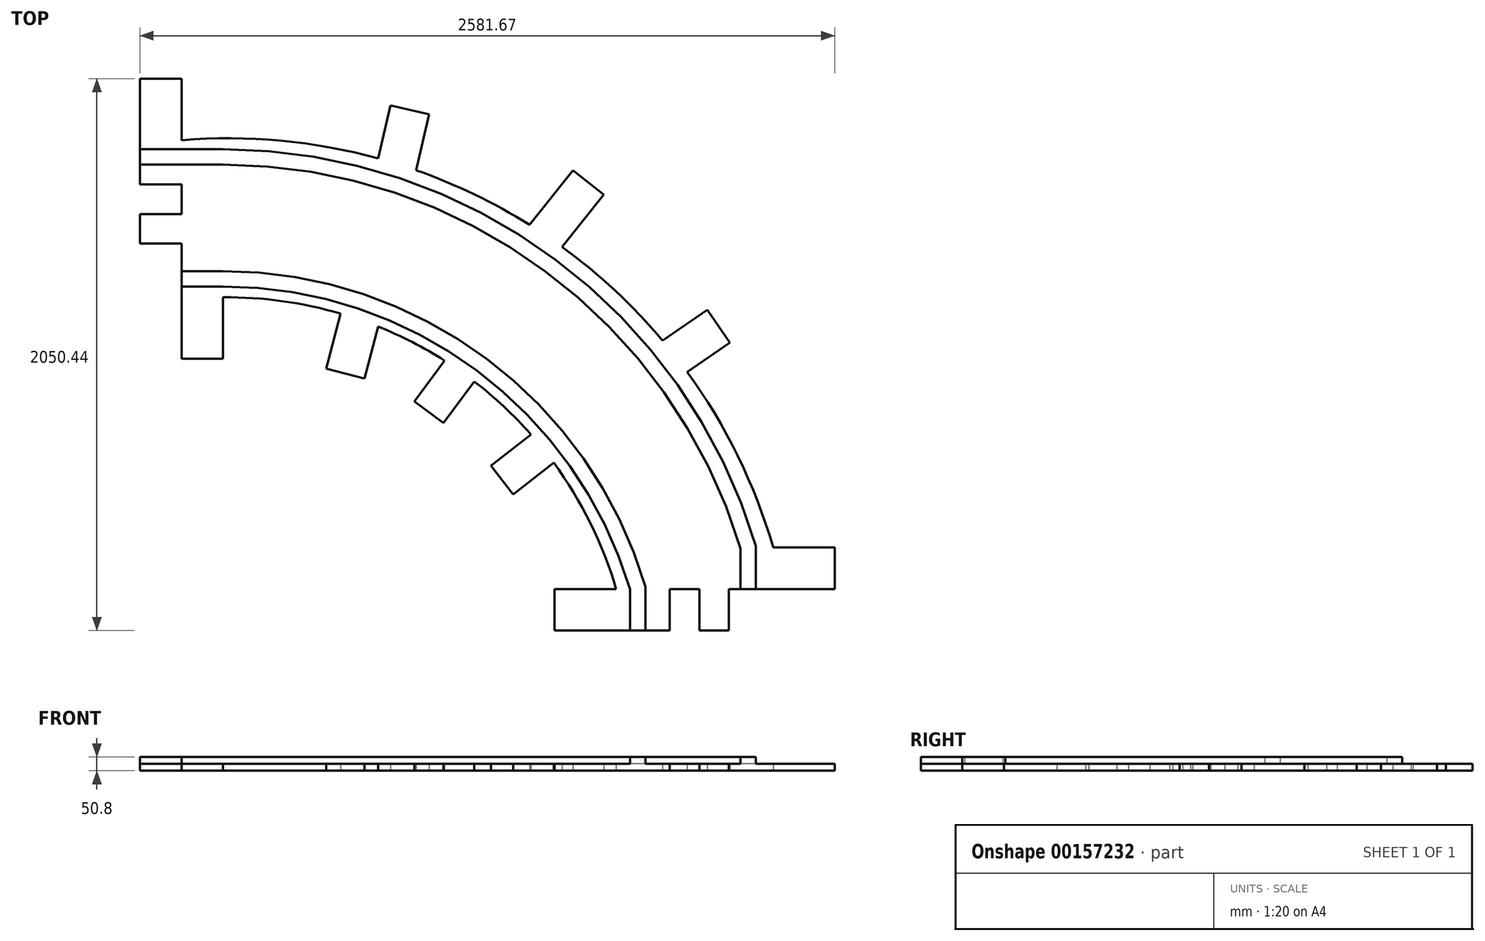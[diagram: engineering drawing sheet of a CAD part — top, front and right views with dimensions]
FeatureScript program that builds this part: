
annotation { "Feature Type Name" : "Feature", "Feature Type Description" : "" }
export const myFeature = defineFeature(function(context is Context, id is Id, definition is map)
    precondition{}
    {
        {
            var Q0;
            Q0=qCreatedBy(makeId("Top.planeOp"),FACE);
            var sketch = newSketch(context, id + "F0", { "sketchPlane" : qUnion([Q0])});
            skLineSegment(sketch, "E0", {"start": v(-123.12, 340.2) * mm, "end": v(-123.12, -52.81) * mm});
            skLineSegment(sketch, "E1", {"start": v(-123.12, -52.81) * mm, "end": v(31.19, -52.81) * mm});
            skLineSegment(sketch, "E2", {"start": v(31.19, -52.81) * mm, "end": v(31.19, -162.82) * mm});
            skLineSegment(sketch, "E3", {"start": v(31.19, -162.82) * mm, "end": v(-123.12, -162.82) * mm});
            skLineSegment(sketch, "E4", {"start": v(-123.12, -162.82) * mm, "end": v(-123.12, -272.82) * mm});
            skLineSegment(sketch, "E5", {"start": v(-123.12, -272.82) * mm, "end": v(31.19, -272.82) * mm});
            skLineSegment(sketch, "E6", {"start": v(31.19, -272.82) * mm, "end": v(31.19, -700.69) * mm});
            skLineSegment(sketch, "E7", {"start": v(2458.55, -1555.94) * mm, "end": v(2065.54, -1555.94) * mm});
            skLineSegment(sketch, "E8", {"start": v(2065.54, -1555.94) * mm, "end": v(2065.54, -1710.24) * mm});
            skLineSegment(sketch, "E9", {"start": v(2065.54, -1710.24) * mm, "end": v(1955.53, -1710.24) * mm});
            skLineSegment(sketch, "E10", {"start": v(1955.53, -1710.24) * mm, "end": v(1955.53, -1555.94) * mm});
            skLineSegment(sketch, "E11", {"start": v(1955.53, -1555.94) * mm, "end": v(1845.52, -1555.94) * mm});
            skLineSegment(sketch, "E12", {"start": v(1845.52, -1555.94) * mm, "end": v(1845.52, -1710.24) * mm});
            skLineSegment(sketch, "E13", {"start": v(1845.52, -1710.24) * mm, "end": v(1417.66, -1710.24) * mm});
            skLineSegment(sketch, "E14", {"start": v(-123.12, 340.2) * mm, "end": v(31.19, 340.2) * mm});
            skLineSegment(sketch, "E15", {"start": v(31.19, 340.2) * mm, "end": v(31.19, 111.7) * mm});
            skLineSegment(sketch, "E16", {"start": v(2458.55, -1555.94) * mm, "end": v(2458.55, -1401.63) * mm});
            skLineSegment(sketch, "E17", {"start": v(2458.55, -1401.63) * mm, "end": v(2230.06, -1401.63) * mm});
            skLineSegment(sketch, "E18", {"start": v(31.19, -700.69) * mm, "end": v(185.5, -700.69) * mm});
            skLineSegment(sketch, "E19", {"start": v(185.5, -700.69) * mm, "end": v(185.5, -472.19) * mm});
            skLineSegment(sketch, "E20", {"start": v(1417.66, -1710.24) * mm, "end": v(1417.66, -1555.94) * mm});
            skLineSegment(sketch, "E21", {"start": v(1417.66, -1555.94) * mm, "end": v(1646.16, -1555.94) * mm});
            skArc(sketch, "E22", {"start": v(2230.06, -1401.63) * mm, "mid": v(1400.55, -252.77) * mm, "end": v(31.19, 111.7) * mm});
            skArc(sketch, "E23", {"start": v(1646.16, -1555.94) * mm, "mid": v(1097.84, -768.75) * mm, "end": v(185.5, -472.19) * mm});
            skLineSegment(sketch, "E24", {"start": v(622.9, -532.64) * mm, "end": v(569.25, -736.82) * mm});
            skLineSegment(sketch, "E25", {"start": v(569.25, -736.82) * mm, "end": v(711.49, -774.2) * mm});
            skLineSegment(sketch, "E26", {"start": v(711.49, -774.2) * mm, "end": v(762.28, -580.9) * mm});
            skLineSegment(sketch, "E27", {"start": v(1008.82, -707.53) * mm, "end": v(896.3, -858.64) * mm});
            skLineSegment(sketch, "E28", {"start": v(896.3, -858.64) * mm, "end": v(1004.64, -939.3) * mm});
            skLineSegment(sketch, "E29", {"start": v(1004.64, -939.3) * mm, "end": v(1119.46, -785.1) * mm});
            skLineSegment(sketch, "E30", {"start": v(1329.87, -981.94) * mm, "end": v(1180.76, -1097.54) * mm});
            skLineSegment(sketch, "E31", {"start": v(1180.76, -1097.54) * mm, "end": v(1263.3, -1204) * mm});
            skLineSegment(sketch, "E32", {"start": v(1263.3, -1204) * mm, "end": v(1414.4, -1086.87) * mm});
            skLineSegment(sketch, "E33", {"start": v(762.28, 43.92) * mm, "end": v(807.94, 241.05) * mm});
            skLineSegment(sketch, "E34", {"start": v(807.94, 241.05) * mm, "end": v(951.13, 207.94) * mm});
            skLineSegment(sketch, "E35", {"start": v(951.13, 207.94) * mm, "end": v(903.05, 0) * mm});
            skLineSegment(sketch, "E36", {"start": v(1324.29, -202.68) * mm, "end": v(1485.87, 0) * mm});
            skLineSegment(sketch, "E37", {"start": v(1485.87, 0) * mm, "end": v(1599.81, -90.84) * mm});
            skLineSegment(sketch, "E38", {"start": v(1599.81, -90.84) * mm, "end": v(1445.4, -284.5) * mm});
            skLineSegment(sketch, "E39", {"start": v(1819.14, -632.88) * mm, "end": v(1985.43, -518.5) * mm});
            skLineSegment(sketch, "E40", {"start": v(1985.43, -518.5) * mm, "end": v(2068.94, -639.9) * mm});
            skLineSegment(sketch, "E41", {"start": v(2068.94, -639.9) * mm, "end": v(1910.13, -749.14) * mm});
            skSolve(sketch);
        }
        {
            var Q0;
            Q0 = qSketchRegion(id + "F0", true);
            extrude(context, id + "F1", {"entities" : qUnion([Q0]), "depth" : 25.4 * mm});
        }
        {
            var Q0;
            Q0=makeQuery(id+"F1.opExtrude","CAP_FACE",FACE,{"disambiguationData":[OSD([sQuery(id+"F0.wireOp",EDGE,"E0"),sQuery(id+"F0.wireOp",EDGE,"E1"),sQuery(id+"F0.wireOp",EDGE,"E2"),sQuery(id+"F0.wireOp",EDGE,"E3"),sQuery(id+"F0.wireOp",EDGE,"E4"),sQuery(id+"F0.wireOp",EDGE,"E5"),sQuery(id+"F0.wireOp",EDGE,"E6"),sQuery(id+"F0.wireOp",EDGE,"E7"),sQuery(id+"F0.wireOp",EDGE,"E8"),sQuery(id+"F0.wireOp",EDGE,"E9"),sQuery(id+"F0.wireOp",EDGE,"E10"),sQuery(id+"F0.wireOp",EDGE,"E11"),sQuery(id+"F0.wireOp",EDGE,"E12"),sQuery(id+"F0.wireOp",EDGE,"E13"),sQuery(id+"F0.wireOp",EDGE,"E14"),sQuery(id+"F0.wireOp",EDGE,"E15"),sQuery(id+"F0.wireOp",EDGE,"E16"),sQuery(id+"F0.wireOp",EDGE,"E17"),sQuery(id+"F0.wireOp",EDGE,"E18"),sQuery(id+"F0.wireOp",EDGE,"E19"),sQuery(id+"F0.wireOp",EDGE,"E20"),sQuery(id+"F0.wireOp",EDGE,"E21"),sQuery(id+"F0.wireOp",EDGE,"E22"),sQuery(id+"F0.wireOp",EDGE,"E23"),sQuery(id+"F0.wireOp",EDGE,"E24"),sQuery(id+"F0.wireOp",EDGE,"E25"),sQuery(id+"F0.wireOp",EDGE,"E26"),sQuery(id+"F0.wireOp",EDGE,"E27"),sQuery(id+"F0.wireOp",EDGE,"E28"),sQuery(id+"F0.wireOp",EDGE,"E29"),sQuery(id+"F0.wireOp",EDGE,"E30"),sQuery(id+"F0.wireOp",EDGE,"E31"),sQuery(id+"F0.wireOp",EDGE,"E32"),sQuery(id+"F0.wireOp",EDGE,"E33"),sQuery(id+"F0.wireOp",EDGE,"E34"),sQuery(id+"F0.wireOp",EDGE,"E35"),sQuery(id+"F0.wireOp",EDGE,"E36"),sQuery(id+"F0.wireOp",EDGE,"E37"),sQuery(id+"F0.wireOp",EDGE,"E38"),sQuery(id+"F0.wireOp",EDGE,"E39"),sQuery(id+"F0.wireOp",EDGE,"E40"),sQuery(id+"F0.wireOp",EDGE,"E41")])],"isStart":false});
            var sketch = newSketch(context, id + "F2", { "sketchPlane" : qUnion([Q0])});
            skLineSegment(sketch, "E42", {"start": v(31.19, -432.08) * mm, "end": v(185.43, -432.08) * mm});
            skLineSegment(sketch, "E43", {"start": v(-123.12, 77.71) * mm, "end": v(185.43, 77.71) * mm});
            skLineSegment(sketch, "E44", {"start": v(2165.73, -1555.94) * mm, "end": v(2165.73, -1396.56) * mm});
            skLineSegment(sketch, "E45", {"start": v(1697.89, -1710.24) * mm, "end": v(1697.89, -1555.94) * mm});
            skArc(sketch, "E46", {"start": v(1697.89, -1555.94) * mm, "mid": v(1127.58, -743.8) * mm, "end": v(185.43, -432.08) * mm});
            skArc(sketch, "E47", {"start": v(2165.73, -1396.56) * mm, "mid": v(1419.83, -331.32) * mm, "end": v(185.43, 77.71) * mm});
            skLineSegment(sketch, "E48.0", {"start": v(-123.12, 20.56) * mm, "end": v(185.43, 20.56) * mm});
            skArc(sketch, "E48.1", {"start": v(2108.58, -1404.99) * mm, "mid": v(1382.37, -374.69) * mm, "end": v(185.43, 20.56) * mm});
            skLineSegment(sketch, "E48.2", {"start": v(2108.58, -1555.94) * mm, "end": v(2108.58, -1404.99) * mm});
            skLineSegment(sketch, "E49.0", {"start": v(31.19, -374.93) * mm, "end": v(185.43, -374.93) * mm});
            skArc(sketch, "E49.1", {"start": v(1755.04, -1547.6) * mm, "mid": v(1165.07, -700.47) * mm, "end": v(185.43, -374.93) * mm});
            skLineSegment(sketch, "E49.2", {"start": v(1755.04, -1710.24) * mm, "end": v(1755.04, -1547.6) * mm});
            skLineSegment(sketch, "E50", {"start": v(31.19, -374.93) * mm, "end": v(31.19, -432.08) * mm});
            skLineSegment(sketch, "E51", {"start": v(-123.12, 77.71) * mm, "end": v(-123.12, 20.56) * mm});
            skLineSegment(sketch, "E52", {"start": v(1697.89, -1710.24) * mm, "end": v(1755.04, -1710.24) * mm});
            skLineSegment(sketch, "E53", {"start": v(2108.58, -1555.94) * mm, "end": v(2165.73, -1555.94) * mm});
            skSolve(sketch);
        }
        {
            var Q0;
            Q0 = qSketchRegion(id + "F2", true);
            extrude(context, id + "F3", {"entities" : qUnion([Q0]), "operationType" : NewBodyOperationType.ADD, "depth" : 25.4 * mm});
        }
    });
